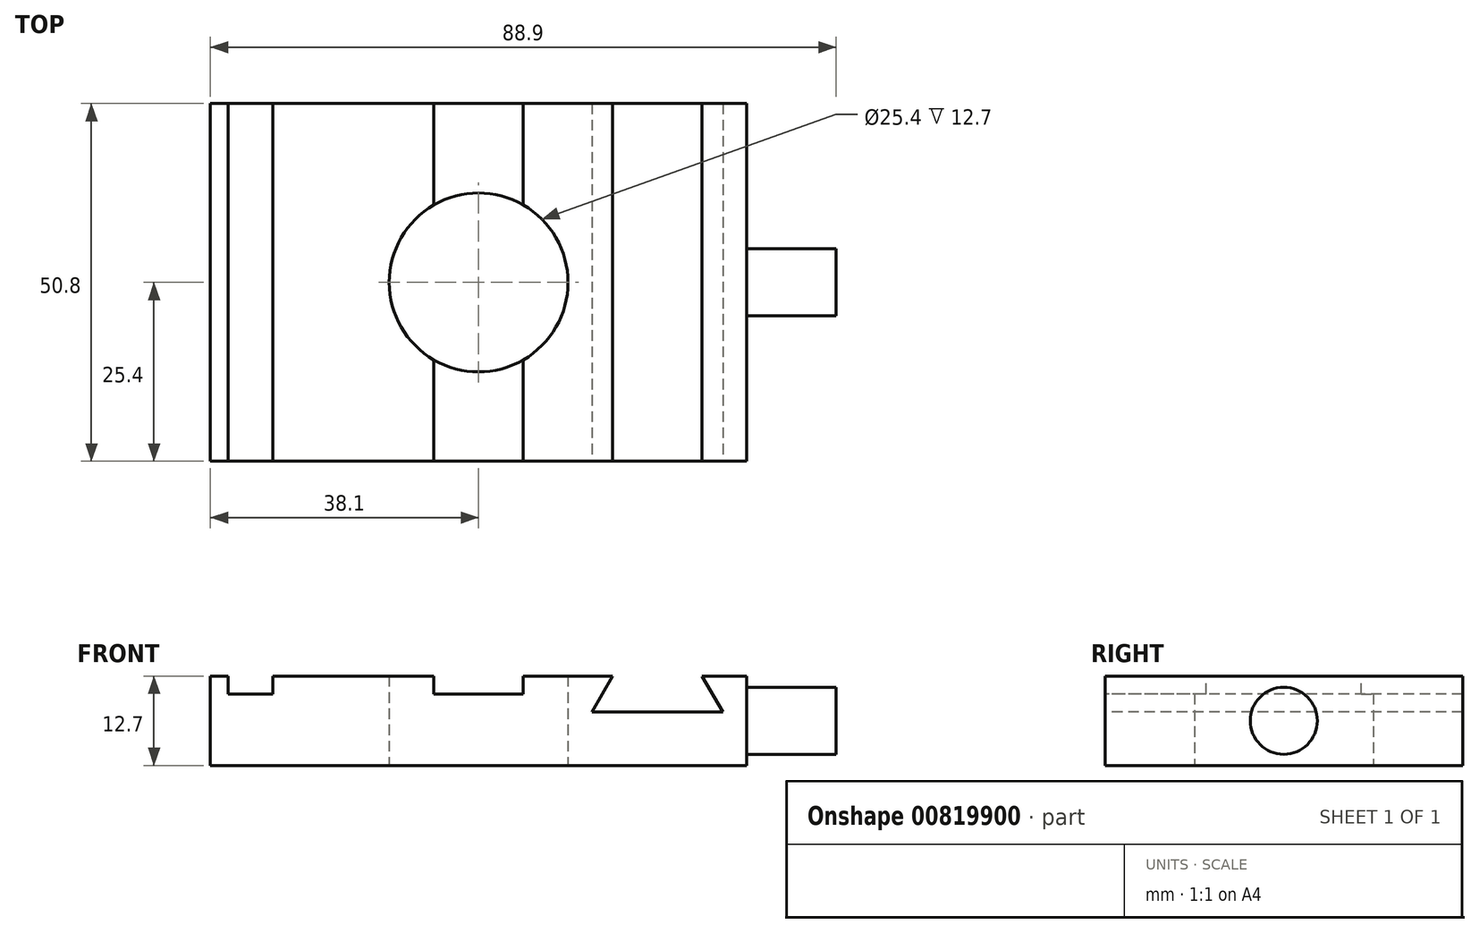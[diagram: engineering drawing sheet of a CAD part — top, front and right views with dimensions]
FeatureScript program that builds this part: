
annotation { "Feature Type Name" : "Feature", "Feature Type Description" : "" }
export const myFeature = defineFeature(function(context is Context, id is Id, definition is map)
    precondition{}
    {
        {
            var Q0;
            Q0=qCreatedBy(makeId("Top.planeOp"),FACE);
            var sketch = newSketch(context, id + "F0", { "sketchPlane" : qUnion([Q0])});
            skLineSegment(sketch, "E0.bottom", {"start": v(38.1, 25.4) * mm, "end": v(-38.1, 25.4) * mm});
            skLineSegment(sketch, "E0.top", {"start": v(38.1, -25.4) * mm, "end": v(-38.1, -25.4) * mm});
            skLineSegment(sketch, "E0.left", {"start": v(38.1, 25.4) * mm, "end": v(38.1, -25.4) * mm});
            skLineSegment(sketch, "E0.right", {"start": v(-38.1, 25.4) * mm, "end": v(-38.1, -25.4) * mm});
            skPoint(sketch, "E0.middle", {"position": v(0, 0) * mm});
            skCircle(sketch, "E1", {"center": v(0, 0) * mm, "radius": 12.7 * mm});
            skSolve(sketch);
        }
        {
            var Q0;
            Q0=makeQuery(id+"F0.imprint","IMPRINT",FACE,{"disambiguationData":[TD([[makeQuery(id+"F0.imprint","IMPRINT",EDGE,{"derivedFrom":sQuery(id+"F0.wireOp",EDGE,"E0.bottom")}),1.0]])]});
            extrude(context, id + "F1", {"entities" : qUnion([Q0]), "depth" : 12.7 * mm, "offsetDistance" : 25.4 * mm});
        }
        {
            var Q0;
            Q0=makeQuery(id+"F1.opExtrude","CAP_FACE",FACE,{"disambiguationData":[OSD([sQuery(id+"F0.wireOp",EDGE,"E0.bottom"),sQuery(id+"F0.wireOp",EDGE,"E0.top"),sQuery(id+"F0.wireOp",EDGE,"E0.left"),sQuery(id+"F0.wireOp",EDGE,"E0.right"),sQuery(id+"F0.wireOp",EDGE,"E1")])],"isStart":false});
            var sketch = newSketch(context, id + "F2", { "sketchPlane" : qUnion([Q0])});
            skLineSegment(sketch, "E2.bottom", {"start": v(-35.56, 25.4) * mm, "end": v(-29.21, 25.4) * mm});
            skLineSegment(sketch, "E2.top", {"start": v(-35.56, -25.4) * mm, "end": v(-29.21, -25.4) * mm});
            skLineSegment(sketch, "E2.left", {"start": v(-35.56, 25.4) * mm, "end": v(-35.56, -25.4) * mm});
            skLineSegment(sketch, "E2.right", {"start": v(-29.21, 25.4) * mm, "end": v(-29.21, -25.4) * mm});
            skLineSegment(sketch, "E3", {"start": v(-6.35, 25.4) * mm, "end": v(-6.35, -25.4) * mm});
            skLineSegment(sketch, "E4", {"start": v(6.35, -25.4) * mm, "end": v(6.35, 25.4) * mm});
            skLineSegment(sketch, "E5", {"start": v(6.35, 25.4) * mm, "end": v(-6.35, 25.4) * mm});
            skLineSegment(sketch, "E6", {"start": v(0, 25.4) * mm, "end": v(0, -25.4) * mm, "construction": true});
            skSolve(sketch);
        }
        {
            var Q0;
            Q0=makeQuery(id+"F2.imprint","IMPRINT",FACE,{"disambiguationData":[TD([[makeQuery(id+"F2.imprint","IMPRINT",EDGE,{"derivedFrom":sQuery(id+"F2.wireOp",EDGE,"E2.bottom")}),1.0]])]});
            var Q1;
            {var subQ0=sQuery(id+"F2.wireOp",EDGE,"E3");var subQ1=makeQuery(id+"F1.opExtrude","CAP_EDGE",EDGE,{"disambiguationData":[OSD([sQuery(id+"F0.wireOp",EDGE,"E0.top")])],"isStart":false});var subQ2=makeQuery(id+"F2.imprint","INTERSECT",VERTEX,{"derivedFrom":[subQ1,subQ0]});Q1=makeQuery(id+"F2.imprint","IMPRINT",FACE,{"disambiguationData":[TD([[makeQuery(id+"F2.imprint","IMPRINT",EDGE,{"disambiguationData":[TD([[subQ2,1.0]])],"derivedFrom":subQ0}),1.0]])]});}
            var Q2;
            {var subQ0=sQuery(id+"F2.wireOp",EDGE,"E5");Q2=makeQuery(id+"F2.imprint","IMPRINT",FACE,{"disambiguationData":[TD([[makeQuery(id+"F2.imprint","IMPRINT",EDGE,{"derivedFrom":subQ0}),1.0]])]});}
            extrude(context, id + "F3", {"entities" : qUnion([Q0, Q1, Q2]), "operationType" : NewBodyOperationType.REMOVE, "oppositeDirection" : true, "depth" : 2.54 * mm, "offsetDistance" : 25.4 * mm});
        }
        {
            var Q0;
            Q0=makeQuery(id+"F1.opExtrude","SWEPT_FACE",FACE,{"disambiguationData":[OSD([sQuery(id+"F0.wireOp",EDGE,"E0.top")])]});
            var sketch = newSketch(context, id + "F4", { "sketchPlane" : qUnion([Q0])});
            skLineSegment(sketch, "E7", {"start": v(19.05, 12.7) * mm, "end": v(16.12, 7.62) * mm});
            skLineSegment(sketch, "E8", {"start": v(16.12, 7.62) * mm, "end": v(34.68, 7.62) * mm});
            skLineSegment(sketch, "E9", {"start": v(34.68, 7.62) * mm, "end": v(31.75, 12.7) * mm});
            skLineSegment(sketch, "E10", {"start": v(31.75, 12.7) * mm, "end": v(19.05, 12.7) * mm});
            skLineSegment(sketch, "E11", {"start": v(25.4, 12.7) * mm, "end": v(25.4, 7.62) * mm, "construction": true});
            skSolve(sketch);
        }
        {
            var Q0;
            Q0=makeQuery(id+"F4.imprint","IMPRINT",FACE,{"disambiguationData":[TD([[makeQuery(id+"F4.imprint","IMPRINT",EDGE,{"derivedFrom":sQuery(id+"F4.wireOp",EDGE,"E7")}),1.0]])]});
            extrude(context, id + "F5", {"entities" : qUnion([Q0]), "operationType" : NewBodyOperationType.REMOVE, "endBound" : BoundingType.THROUGH_ALL, "oppositeDirection" : true, "depth" : 25.4 * mm, "offsetDistance" : 25.4 * mm});
        }
        {
            var Q0;
            Q0=makeQuery(id+"F1.opExtrude","SWEPT_FACE",FACE,{"disambiguationData":[OSD([sQuery(id+"F0.wireOp",EDGE,"E0.left")])]});
            var sketch = newSketch(context, id + "F6", { "sketchPlane" : qUnion([Q0])});
            skCircle(sketch, "E12", {"center": v(0, 6.35) * mm, "radius": 4.76 * mm});
            skPoint(sketch, "E12.centerSnap0", {"position": v(-25.4, 6.35) * mm});
            skPoint(sketch, "E12.centerSnap1", {"position": v(0, 12.7) * mm});
            skSolve(sketch);
        }
        {
            var Q0;
            Q0=makeQuery(id+"F6.imprint","IMPRINT",FACE,{"disambiguationData":[TD([[makeQuery(id+"F6.imprint","IMPRINT",EDGE,{"derivedFrom":sQuery(id+"F6.wireOp",EDGE,"E12")}),1.0]])]});
            extrude(context, id + "F7", {"entities" : qUnion([Q0]), "operationType" : NewBodyOperationType.ADD, "depth" : 12.7 * mm, "offsetDistance" : 25.4 * mm});
        }
    });
